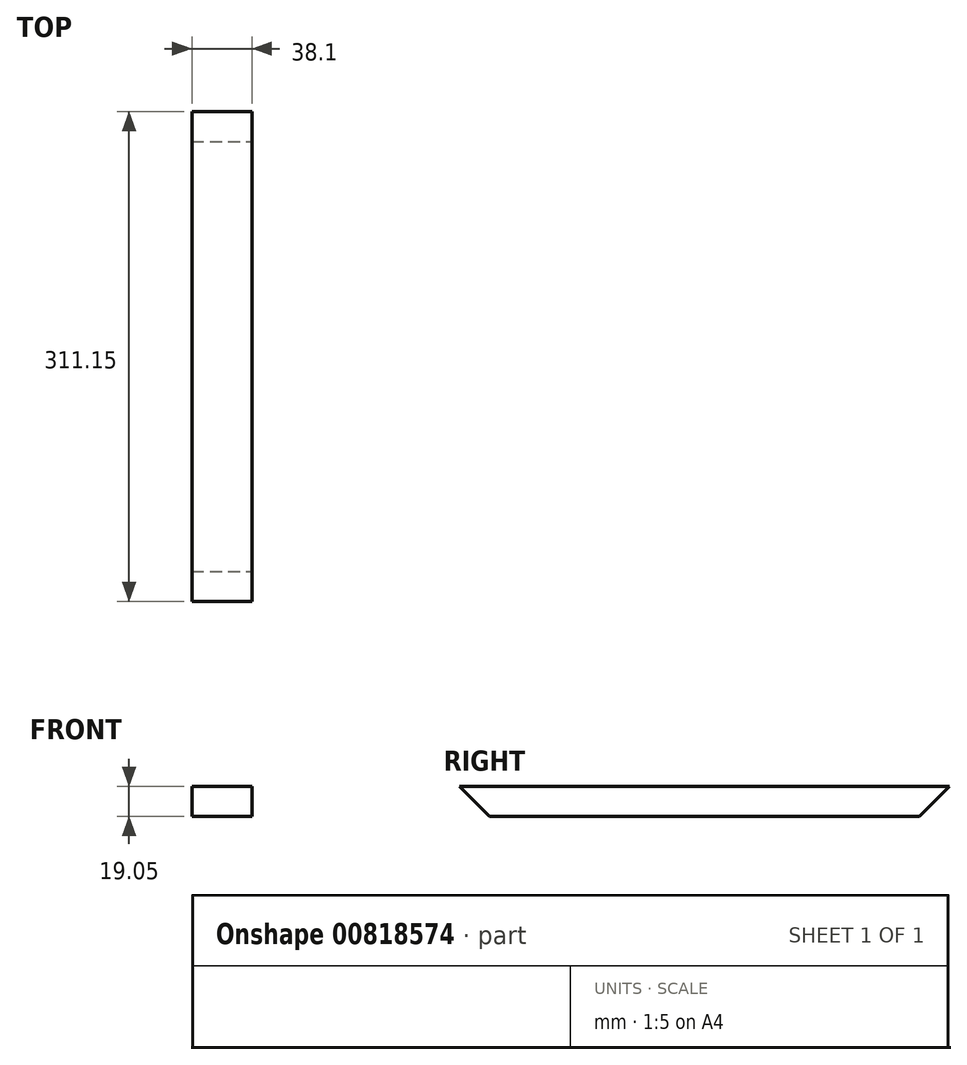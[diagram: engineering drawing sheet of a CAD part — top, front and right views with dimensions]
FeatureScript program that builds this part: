
annotation { "Feature Type Name" : "Feature", "Feature Type Description" : "" }
export const myFeature = defineFeature(function(context is Context, id is Id, definition is map)
    precondition{}
    {
        {
            var Q0;
            Q0=qCreatedBy(makeId("Front.planeOp"),FACE);
            var sketch = newSketch(context, id + "F0", { "sketchPlane" : qUnion([Q0])});
            skLineSegment(sketch, "E0.bottom", {"start": v(-12.82, 8.22) * mm, "end": v(25.28, 8.22) * mm});
            skLineSegment(sketch, "E0.top", {"start": v(-12.82, -10.83) * mm, "end": v(25.28, -10.83) * mm});
            skLineSegment(sketch, "E0.left", {"start": v(-12.82, 8.22) * mm, "end": v(-12.82, -10.83) * mm});
            skLineSegment(sketch, "E0.right", {"start": v(25.28, 8.22) * mm, "end": v(25.28, -10.83) * mm});
            skSolve(sketch);
        }
        {
            var Q0;
            Q0=qSketchRegion(id+"F0",true);
            extrude(context, id + "F1", {"entities" : qUnion([Q0]), "depth" : 311.15 * mm, "offsetDistance" : 25.4 * mm});
        }
        {
            var Q0;
            Q0=makeQuery(id+"F1.opExtrude","SWEPT_FACE",FACE,{"disambiguationData":[OSD([sQuery(id+"F0.wireOp",EDGE,"E0.right")])]});
            var sketch = newSketch(context, id + "F2", { "sketchPlane" : qUnion([Q0])});
            skLineSegment(sketch, "E1", {"start": v(-311.15, 8.22) * mm, "end": v(-292.1, -10.83) * mm});
            skLineSegment(sketch, "E2", {"start": v(-292.1, -10.83) * mm, "end": v(-311.15, -10.83) * mm});
            skLineSegment(sketch, "E3", {"start": v(-311.15, -10.83) * mm, "end": v(-311.15, 8.22) * mm});
            skLineSegment(sketch, "E4", {"start": v(0, 8.22) * mm, "end": v(-19.05, -10.83) * mm});
            skLineSegment(sketch, "E5", {"start": v(-19.05, -10.83) * mm, "end": v(0, -10.83) * mm});
            skLineSegment(sketch, "E6", {"start": v(0, -10.83) * mm, "end": v(0, 8.22) * mm});
            skSolve(sketch);
        }
        {
            var Q0;
            Q0=qSketchRegion(id+"F2",true);
            extrude(context, id + "F3", {"entities" : qUnion([Q0]), "operationType" : NewBodyOperationType.REMOVE, "oppositeDirection" : true, "depth" : 38.1 * mm, "offsetDistance" : 25.4 * mm});
        }
    });
